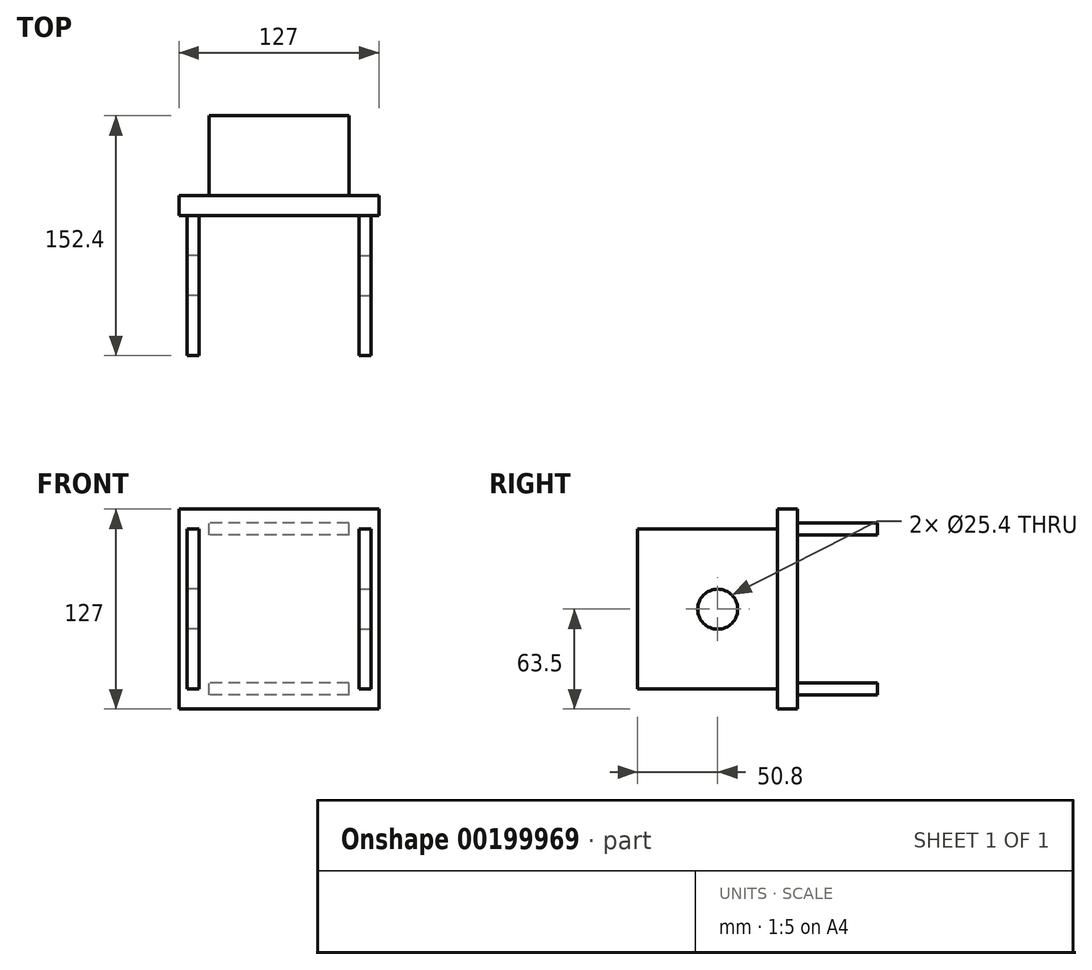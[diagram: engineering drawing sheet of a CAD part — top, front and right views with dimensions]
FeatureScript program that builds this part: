
annotation { "Feature Type Name" : "Feature", "Feature Type Description" : "" }
export const myFeature = defineFeature(function(context is Context, id is Id, definition is map)
    precondition{}
    {
        {
            var Q0;
            Q0=qCreatedBy(makeId("Front.planeOp"),FACE);
            var sketch = newSketch(context, id + "F0", { "sketchPlane" : qUnion([Q0])});
            skLineSegment(sketch, "E0.bottom", {"start": v(63.5, -63.5) * mm, "end": v(-63.5, -63.5) * mm});
            skLineSegment(sketch, "E0.top", {"start": v(63.5, 63.5) * mm, "end": v(-63.5, 63.5) * mm});
            skLineSegment(sketch, "E0.left", {"start": v(63.5, -63.5) * mm, "end": v(63.5, 63.5) * mm});
            skLineSegment(sketch, "E0.right", {"start": v(-63.5, -63.5) * mm, "end": v(-63.5, 63.5) * mm});
            skPoint(sketch, "E0.middle", {"position": v(0, 0) * mm});
            skLineSegment(sketch, "E1.bottom", {"start": v(-50.8, -50.8) * mm, "end": v(-58.42, -50.8) * mm});
            skLineSegment(sketch, "E1.top", {"start": v(-50.8, 50.8) * mm, "end": v(-58.42, 50.8) * mm});
            skLineSegment(sketch, "E1.left", {"start": v(-50.8, -50.8) * mm, "end": v(-50.8, 50.8) * mm});
            skLineSegment(sketch, "E1.right", {"start": v(-58.42, -50.8) * mm, "end": v(-58.42, 50.8) * mm});
            skPoint(sketch, "E1.middle", {"position": v(-54.6, 0) * mm});
            skSolve(sketch);
        }
        {
            var Q0;
            Q0=makeQuery(id+"F0.imprint","IMPRINT",FACE,{"disambiguationData":[TD([[makeQuery(id+"F0.imprint","IMPRINT",EDGE,{"derivedFrom":sQuery(id+"F0.wireOp",EDGE,"E1.bottom")}),-1.0]])]});
            extrude(context, id + "F1", {"entities" : qUnion([Q0]), "depth" : 101.6 * mm});
        }
        {
            var Q0;
            Q0=makeQuery(id+"F1.opExtrude","SWEPT_FACE",FACE,{"disambiguationData":[OSD([sQuery(id+"F0.wireOp",EDGE,"E1.right")])]});
            var sketch = newSketch(context, id + "F2", { "sketchPlane" : qUnion([Q0])});
            skCircle(sketch, "E2", {"center": v(50.8, 0) * mm, "radius": 12.7 * mm});
            skPoint(sketch, "E2.centerSnap0", {"position": v(0, 0) * mm});
            skSolve(sketch);
        }
        {
            var Q0;
            Q0=makeQuery(id+"F2.imprint","IMPRINT",FACE,{"disambiguationData":[TD([[makeQuery(id+"F2.imprint","IMPRINT",EDGE,{"derivedFrom":sQuery(id+"F2.wireOp",EDGE,"E2")}),1.0]])]});
            extrude(context, id + "F3", {"entities" : qUnion([Q0]), "operationType" : NewBodyOperationType.REMOVE, "endBound" : BoundingType.THROUGH_ALL, "oppositeDirection" : true, "depth" : 25.4 * mm});
        }
        {
            var Q0;
            Q0=makeQuery(id+"F0.imprint","IMPRINT",FACE,{"disambiguationData":[TD([[makeQuery(id+"F0.imprint","IMPRINT",EDGE,{"derivedFrom":sQuery(id+"F0.wireOp",EDGE,"E0.bottom")}),-1.0]])]});
            var sketch = newSketch(context, id + "F4", { "sketchPlane" : qUnion([Q0])});
            skLineSegment(sketch, "E3.bottom", {"start": v(58.42, 50.8) * mm, "end": v(50.8, 50.8) * mm});
            skLineSegment(sketch, "E3.top", {"start": v(58.42, -50.8) * mm, "end": v(50.8, -50.8) * mm});
            skLineSegment(sketch, "E3.left", {"start": v(58.42, 50.8) * mm, "end": v(58.42, -50.8) * mm});
            skLineSegment(sketch, "E3.right", {"start": v(50.8, 50.8) * mm, "end": v(50.8, -50.8) * mm});
            skPoint(sketch, "E3.middle", {"position": v(54.6, 0) * mm});
            skSolve(sketch);
        }
        {
            var Q0;
            Q0 = qSketchRegion(id + "F4", true);
            extrude(context, id + "F5", {"entities" : qUnion([Q0]), "depth" : 101.6 * mm});
        }
        {
            var Q0;
            Q0=makeQuery(id+"F5.opExtrude","SWEPT_FACE",FACE,{"disambiguationData":[OSD([sQuery(id+"F4.wireOp",EDGE,"E3.left")])]});
            var sketch = newSketch(context, id + "F6", { "sketchPlane" : qUnion([Q0])});
            skCircle(sketch, "E4", {"center": v(-50.8, 0) * mm, "radius": 12.7 * mm});
            skSolve(sketch);
        }
        {
            var Q0;
            Q0=makeQuery(id+"F6.imprint","IMPRINT",FACE,{"disambiguationData":[TD([[makeQuery(id+"F6.imprint","IMPRINT",EDGE,{"derivedFrom":sQuery(id+"F6.wireOp",EDGE,"E4")}),1.0]])]});
            extrude(context, id + "F7", {"entities" : qUnion([Q0]), "operationType" : NewBodyOperationType.REMOVE, "endBound" : BoundingType.THROUGH_ALL, "oppositeDirection" : true, "depth" : 25.4 * mm});
        }
        {
            var Q0;
            Q0=makeQuery(id+"F0.imprint","IMPRINT",FACE,{"disambiguationData":[TD([[makeQuery(id+"F0.imprint","IMPRINT",EDGE,{"derivedFrom":sQuery(id+"F0.wireOp",EDGE,"E0.bottom")}),-1.0]])]});
            var sketch = newSketch(context, id + "F8", { "sketchPlane" : qUnion([Q0])});
            skLineSegment(sketch, "E5.bottom", {"start": v(44.45, 46.99) * mm, "end": v(-44.45, 46.99) * mm});
            skLineSegment(sketch, "E5.top", {"start": v(44.45, 54.6) * mm, "end": v(-44.45, 54.61) * mm});
            skLineSegment(sketch, "E5.left", {"start": v(44.45, 46.99) * mm, "end": v(44.45, 54.61) * mm});
            skLineSegment(sketch, "E5.right", {"start": v(-44.45, 46.99) * mm, "end": v(-44.45, 54.61) * mm});
            skPoint(sketch, "E5.middle", {"position": v(0, 50.8) * mm});
            skLineSegment(sketch, "E6.bottom", {"start": v(44.45, -54.61) * mm, "end": v(-44.45, -54.6) * mm});
            skLineSegment(sketch, "E6.top", {"start": v(44.45, -47) * mm, "end": v(-44.45, -46.99) * mm});
            skLineSegment(sketch, "E6.left", {"start": v(44.45, -54.61) * mm, "end": v(44.45, -46.99) * mm});
            skLineSegment(sketch, "E6.right", {"start": v(-44.45, -54.61) * mm, "end": v(-44.45, -46.99) * mm});
            skPoint(sketch, "E6.middle", {"position": v(0, -50.8) * mm});
            skSolve(sketch);
        }
        {
            var Q0;
            Q0 = qSketchRegion(id + "F8", true);
            extrude(context, id + "F9", {"entities" : qUnion([Q0]), "oppositeDirection" : true, "depth" : 50.8 * mm});
        }
        {
            var Q0;
            Q0=makeQuery(id+"F0.imprint","IMPRINT",FACE,{"disambiguationData":[TD([[makeQuery(id+"F0.imprint","IMPRINT",EDGE,{"derivedFrom":sQuery(id+"F0.wireOp",EDGE,"E0.bottom")}),-1.0]])]});
            extrude(context, id + "F10", {"entities" : qUnion([Q0]), "operationType" : NewBodyOperationType.ADD, "depth" : 12.7 * mm});
        }
    });
